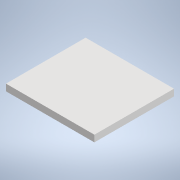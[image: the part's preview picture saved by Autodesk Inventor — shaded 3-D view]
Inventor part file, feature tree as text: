
AUTODESK INVENTOR PART (.ipt)
format: ipt  version: 2020 (Build 240168000, 168)  size: 93,696 bytes
history: native  units: mm
features: extrude x1, sketch x1
ambient origin geometry x8: Origin, YZ Plane, XZ Plane, XY Plane, X Axis, Y Axis, Z Axis, Center Point
bodies: Solid1 (feature_tree)
feature tree (2):
  extrude  "Extrusion1"  Depth=30.0mm
  sketch  "Sketch1"  dims[d0=33.3mm d1=30.0mm d2=2.5mm d3=0.0mm]
